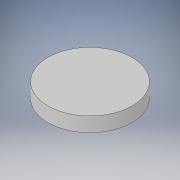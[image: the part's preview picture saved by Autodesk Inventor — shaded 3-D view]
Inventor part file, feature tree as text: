
AUTODESK INVENTOR PART (.ipt)
format: ipt  version: 2018 (Build 220112000, 112)  size: 89,600 bytes
history: native  units: in
note: dims shown in document units (in); Inventor stores cm internally (conversion verified against a paired STEP export)
features: extrude x1, sketch x1
ambient origin geometry x8: Origin, YZ Plane, XZ Plane, XY Plane, X Axis, Y Axis, Z Axis, Center Point
bodies: Solid1 (feature_tree)
feature tree (2):
  extrude  "Extrusion1"  Depth=0.1898in TaperAngle=0.0deg
  sketch  "Sketch1"  dims[d0=1.1024in d1=0.1898in d2=0.0in]
